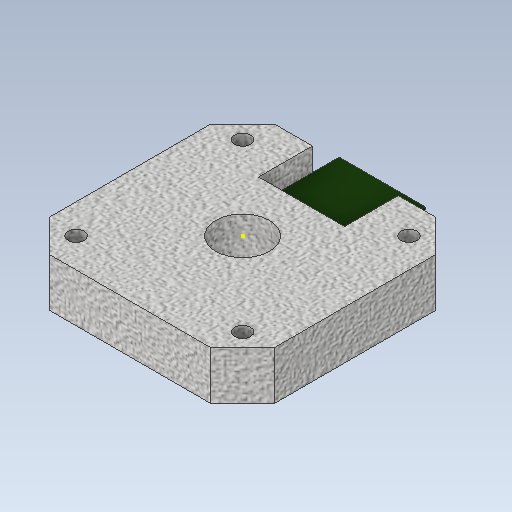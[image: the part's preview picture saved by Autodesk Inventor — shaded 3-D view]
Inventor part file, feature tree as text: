
AUTODESK INVENTOR PART (.ipt)
format: ipt  version: 2020 (Build 240168000, 168)  size: 332,288 bytes
history: native  units: mm
features: sketch x9, extrude x7, mirror x4, projected_geometry x3, chamfer x1, fillet x1
ambient origin geometry x8: Origin, YZ Plane, XZ Plane, XY Plane, X Axis, Y Axis, Z Axis, Center Point
bodies: Solid1 (feature_tree)
feature tree (25):
  extrude  "Extrusion1"  Depth=42.0mm
  chamfer  "Chamfer1"  Distance=9.0mm
  sketch  "Sketch2"  dims[d4=6.0mm d5=2.0mm d6=45.0deg d7=10.0mm]
  extrude  "Extrusion2"  Depth=10.0mm
  extrude  "Extrusion3"  Depth=3.0mm
  mirror  "Mirror1"
  mirror  "Mirror2"
  extrude  "Extrusion5"  Depth=5.5mm
  fillet  "Fillet1"  Radius=22.0mm
  extrude  "Extrusion6"  Depth=16.0mm
  extrude  "Extrusion7"  Depth=4.0mm
  sketch  "Sketch9"  dims[d28=0.5mm]
  extrude  "Extrusion8"  Depth=10.0mm TaperAngle=0.0deg
  mirror  "Mirror3"
  mirror  "Mirror4"
  sketch  "Sketch1"  dims[d0=42.0mm d1=42.0mm d2=9.0mm d3=0.0mm]
  sketch  "Sketch3"  dims[d8=22.0mm d9=0.0mm d10=3.0mm]
  sketch  "Sketch4"  dims[d11=5.5mm d12=5.5mm d13=22.0mm d14=0.0mm]
  sketch  "Sketch6"  dims[d20=16.0mm d21=8.0mm]
  projected_geometry  "Projected Loop1"
  sketch  "Sketch7"  dims[d22=4.0mm d23=0.0mm d24=4.0mm]
  projected_geometry  "Projected Loop2"
  sketch  "Sketch8"  dims[d25=0.5mm d26=10.0mm d27=0.0mm]
  projected_geometry  "Projected Loop3"
  sketch  "Sketch10"  dims[d29=0.2mm d30=15.0mm d31=0.0mm d32=6.0mm d33=3.0mm d34=0.0mm]
